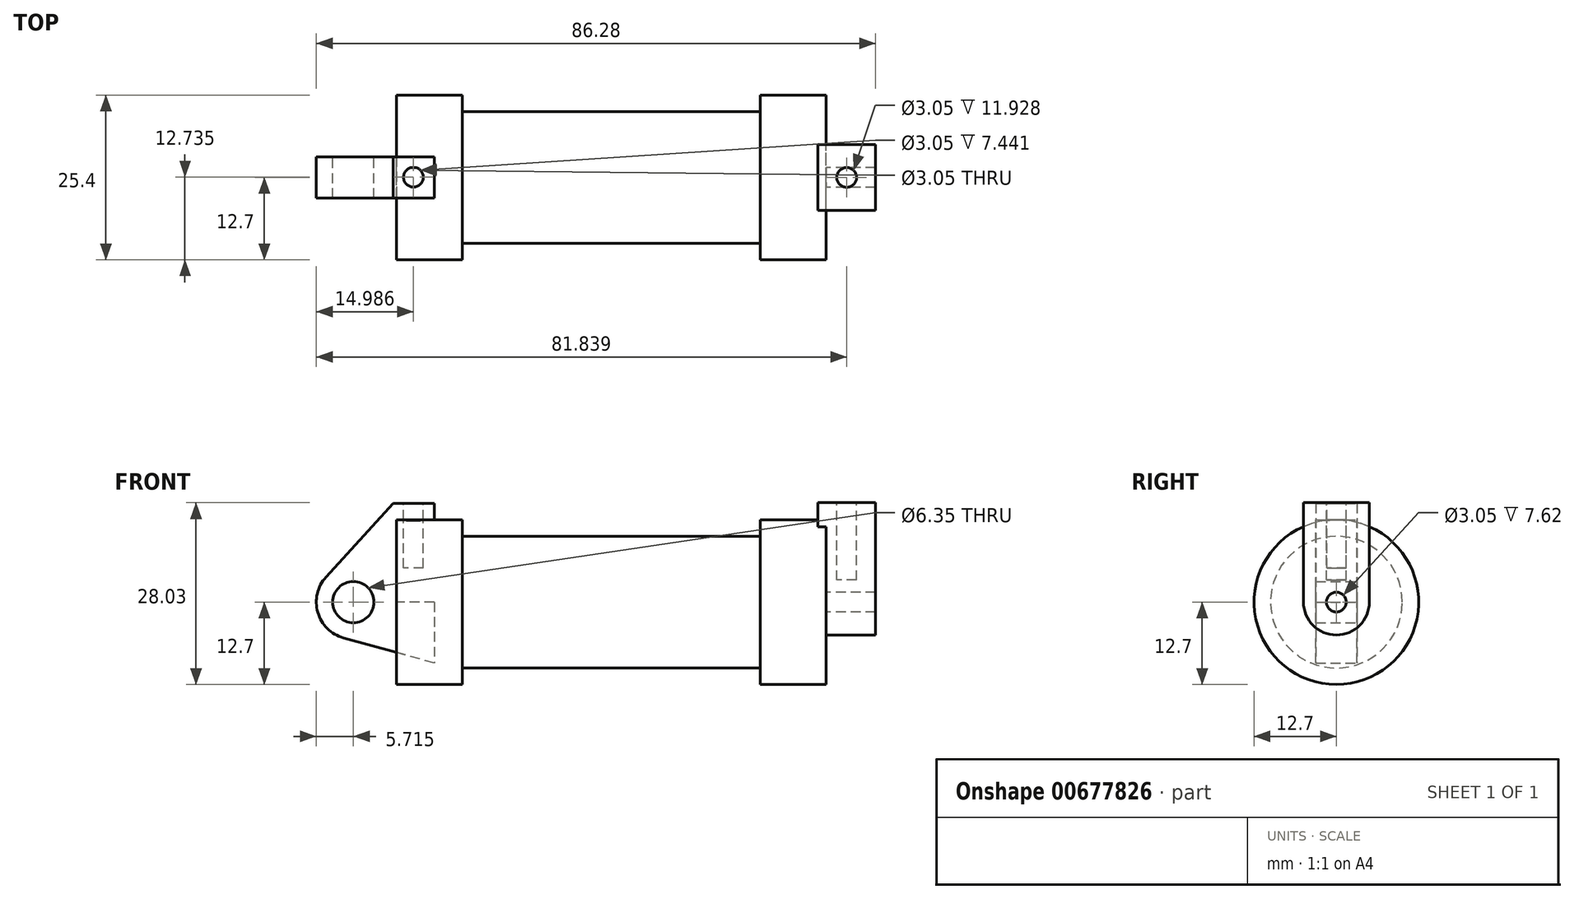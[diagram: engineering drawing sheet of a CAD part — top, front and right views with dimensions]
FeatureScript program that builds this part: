
annotation { "Feature Type Name" : "Feature", "Feature Type Description" : "" }
export const myFeature = defineFeature(function(context is Context, id is Id, definition is map)
    precondition{}
    {
        {
            var Q0;
            Q0=qCreatedBy(makeId("Front.planeOp"),FACE);
            var sketch = newSketch(context, id + "F0", { "sketchPlane" : qUnion([Q0])});
            skLineSegment(sketch, "E0", {"start": v(0, 0) * mm, "end": v(0, 12.7) * mm});
            skLineSegment(sketch, "E1", {"start": v(0, 12.7) * mm, "end": v(10.16, 12.7) * mm});
            skLineSegment(sketch, "E2", {"start": v(10.16, 12.7) * mm, "end": v(10.16, 10.16) * mm});
            skLineSegment(sketch, "E3", {"start": v(10.16, 10.16) * mm, "end": v(56.13, 10.16) * mm});
            skLineSegment(sketch, "E4", {"start": v(56.13, 10.16) * mm, "end": v(56.13, 12.7) * mm});
            skLineSegment(sketch, "E5", {"start": v(56.13, 12.7) * mm, "end": v(66.3, 12.7) * mm});
            skLineSegment(sketch, "E6", {"start": v(66.3, 12.7) * mm, "end": v(66.3, 0) * mm});
            skLineSegment(sketch, "E7", {"start": v(66.3, 0) * mm, "end": v(0, 0) * mm});
            skLineSegment(sketch, "E8", {"start": v(5.84, 15.24) * mm, "end": v(-0.5, 15.24) * mm});
            skLineSegment(sketch, "E9", {"start": v(-0.5, 15.24) * mm, "end": v(-10.88, 3.85) * mm});
            skLineSegment(sketch, "E10", {"start": v(0, 0) * mm, "end": v(-6.65, 0) * mm});
            skCircle(sketch, "E11", {"center": v(-6.65, 0) * mm, "radius": 5.72 * mm});
            skCircle(sketch, "E12", {"center": v(-6.65, 0) * mm, "radius": 3.18 * mm});
            skLineSegment(sketch, "E13", {"start": v(5.84, 15.24) * mm, "end": v(5.84, -9.4) * mm});
            skLineSegment(sketch, "E14", {"start": v(5.84, -9.4) * mm, "end": v(-8.18, -5.5) * mm});
            skSolve(sketch);
        }
        {
            var Q0;
            {var subQ0=sQuery(id+"F0.wireOp",EDGE,"E2");Q0=makeQuery(id+"F0.imprint","IMPRINT",FACE,{"disambiguationData":[TD([[makeQuery(id+"F0.imprint","IMPRINT",EDGE,{"derivedFrom":subQ0}),-1.0]])]});}
            var sketch = newSketch(context, id + "F1", { "sketchPlane" : qUnion([Q0])});
            skSolve(sketch);
        }
        {
            var Q0;
            Q0 = qSketchRegion(id + "F1", true);
            var Q1;
            {var subQ0=sQuery(id+"F0.wireOp",EDGE,"E2");Q1=makeQuery(id+"F0.imprint","IMPRINT",FACE,{"disambiguationData":[TD([[makeQuery(id+"F0.imprint","IMPRINT",EDGE,{"derivedFrom":subQ0}),-1.0]])]});}
            var Q2;
            {var subQ0=sQuery(id+"F0.wireOp",EDGE,"E0");Q2=makeQuery(id+"F0.imprint","IMPRINT",FACE,{"disambiguationData":[TD([[makeQuery(id+"F0.imprint","IMPRINT",EDGE,{"derivedFrom":subQ0}),-1.0]])]});}
            var Q3;
            Q3=sQuery(id+"F0.wireOp",EDGE,"E7");
            revolve(context, id + "F2", {"entities" : qUnion([Q0, Q1, Q2]), "axis" : qUnion([Q3]), "revolveType" : RevolveType.FULL});
        }
        {
            var Q0;
            {var subQ1=sQuery(id+"F0.wireOp",EDGE,"E0");Q0=makeQuery(id+"F0.imprint","IMPRINT",FACE,{"disambiguationData":[TD([[makeQuery(id+"F0.imprint","IMPRINT",EDGE,{"derivedFrom":subQ1}),1.0]])]});}
            var Q1;
            {var subQ0=sQuery(id+"F0.wireOp",EDGE,"E14");Q1=makeQuery(id+"F0.imprint","IMPRINT",FACE,{"disambiguationData":[TD([[makeQuery(id+"F0.imprint","IMPRINT",EDGE,{"derivedFrom":subQ0}),-1.0]])]});}
            var Q2;
            {var subQ5=sQuery(id+"F0.wireOp",EDGE,"E12");Q2=makeQuery(id+"F0.imprint","IMPRINT",FACE,{"disambiguationData":[TD([[makeQuery(id+"F0.imprint","IMPRINT",EDGE,{"derivedFrom":subQ5}),-1.0]])]});}
            extrude(context, id + "F3", {"entities" : qUnion([Q0, Q1, Q2]), "endBound" : BoundingType.SYMMETRIC, "depth" : 6.35 * mm, "offsetDistance" : 25.4 * mm});
        }
        {
            var Q0;
            Q0=makeQuery(id+"F2.opRevolve","SWEPT_FACE",FACE,{"disambiguationData":[OSD([sQuery(id+"F0.wireOp",EDGE,"E6")])]});
            var sketch = newSketch(context, id + "F4", { "sketchPlane" : qUnion([Q0])});
            skCircle(sketch, "E15", {"center": v(0, 0) * mm, "radius": 1.52 * mm});
            skCircle(sketch, "E16", {"center": v(0, 0) * mm, "radius": 5.08 * mm});
            skLineSegment(sketch, "E17", {"start": v(5.08, 0) * mm, "end": v(5.08, 15.33) * mm});
            skLineSegment(sketch, "E18", {"start": v(5.08, 15.33) * mm, "end": v(-5.08, 15.33) * mm});
            skLineSegment(sketch, "E19", {"start": v(-5.08, 15.33) * mm, "end": v(-5.08, 0) * mm});
            skSolve(sketch);
        }
        {
            var Q0;
            Q0 = qSketchRegion(id + "F4", true);
            extrude(context, id + "F5", {"entities" : qUnion([Q0]), "operationType" : NewBodyOperationType.ADD, "depth" : 7.62 * mm, "offsetDistance" : 25.4 * mm});
        }
        {
            var Q0;
            Q0=makeQuery(id+"F5.opExtrude","CAP_FACE",FACE,{"disambiguationData":[OSD([sQuery(id+"F4.wireOp",EDGE,"E15"),sQuery(id+"F4.wireOp",EDGE,"E16"),sQuery(id+"F4.wireOp",EDGE,"E17"),sQuery(id+"F4.wireOp",EDGE,"E18"),sQuery(id+"F4.wireOp",EDGE,"E19")])],"isStart":true});
            extrude(context, id + "F6", {"entities" : qUnion([Q0]), "operationType" : NewBodyOperationType.ADD, "depth" : 1.27 * mm, "offsetDistance" : 25.4 * mm});
        }
        {
            var Q0;
            Q0=makeQuery(id+"F3.opExtrude","SWEPT_FACE",FACE,{"disambiguationData":[OSD([sQuery(id+"F0.wireOp",EDGE,"E8")])]});
            var sketch = newSketch(context, id + "F7", { "sketchPlane" : qUnion([Q0])});
            skCircle(sketch, "E20", {"center": v(2.62, 0.03) * mm, "radius": 1.52 * mm});
            skSolve(sketch);
        }
        {
            var Q0;
            {var subQ0=sQuery(id+"F4.wireOp",EDGE,"E18");Q0=makeQuery(id+"F6.boolean.opBoolean","MERGE",FACE,{"derivedFrom":[makeQuery(id+"F5.opExtrude","SWEPT_FACE",FACE,{"disambiguationData":[OSD([subQ0])]}),makeQuery(id+"F6.opExtrude","SWEPT_FACE",FACE,{"disambiguationData":[OSD([subQ0])]})]});}
            var sketch = newSketch(context, id + "F8", { "sketchPlane" : qUnion([Q0])});
            skPoint(sketch, "E21.orphan", {"position": v(73.91, 0) * mm});
            skPoint(sketch, "E22.end.orphan", {"position": v(65.02, 0) * mm});
            skPoint(sketch, "E23.center.orphan", {"position": v(69.47, 0) * mm});
            skCircle(sketch, "E24", {"center": v(69.47, 0) * mm, "radius": 1.52 * mm});
            skSolve(sketch);
        }
        {
            var Q0;
            Q0 = qSketchRegion(id + "F8", true);
            extrude(context, id + "F9", {"entities" : qUnion([Q0]), "operationType" : NewBodyOperationType.ADD, "oppositeDirection" : true, "depth" : 10.4 * mm, "offsetDistance" : 25.4 * mm});
        }
        {
            var Q0;
            Q0=makeQuery(id+"F8.imprint","IMPRINT",FACE,{"disambiguationData":[TD([[makeQuery(id+"F8.imprint","IMPRINT",EDGE,{"derivedFrom":sQuery(id+"F8.wireOp",EDGE,"E24")}),1.0]])]});
            extrude(context, id + "F10", {"entities" : qUnion([Q0]), "operationType" : NewBodyOperationType.REMOVE, "oppositeDirection" : true, "depth" : 11.93 * mm, "offsetDistance" : 25.4 * mm});
        }
        {
            var Q0;
            Q0 = qSketchRegion(id + "F7", true);
            extrude(context, id + "F11", {"entities" : qUnion([Q0]), "operationType" : NewBodyOperationType.REMOVE, "oppositeDirection" : true, "depth" : 9.98 * mm, "offsetDistance" : 25.4 * mm});
        }
    });
